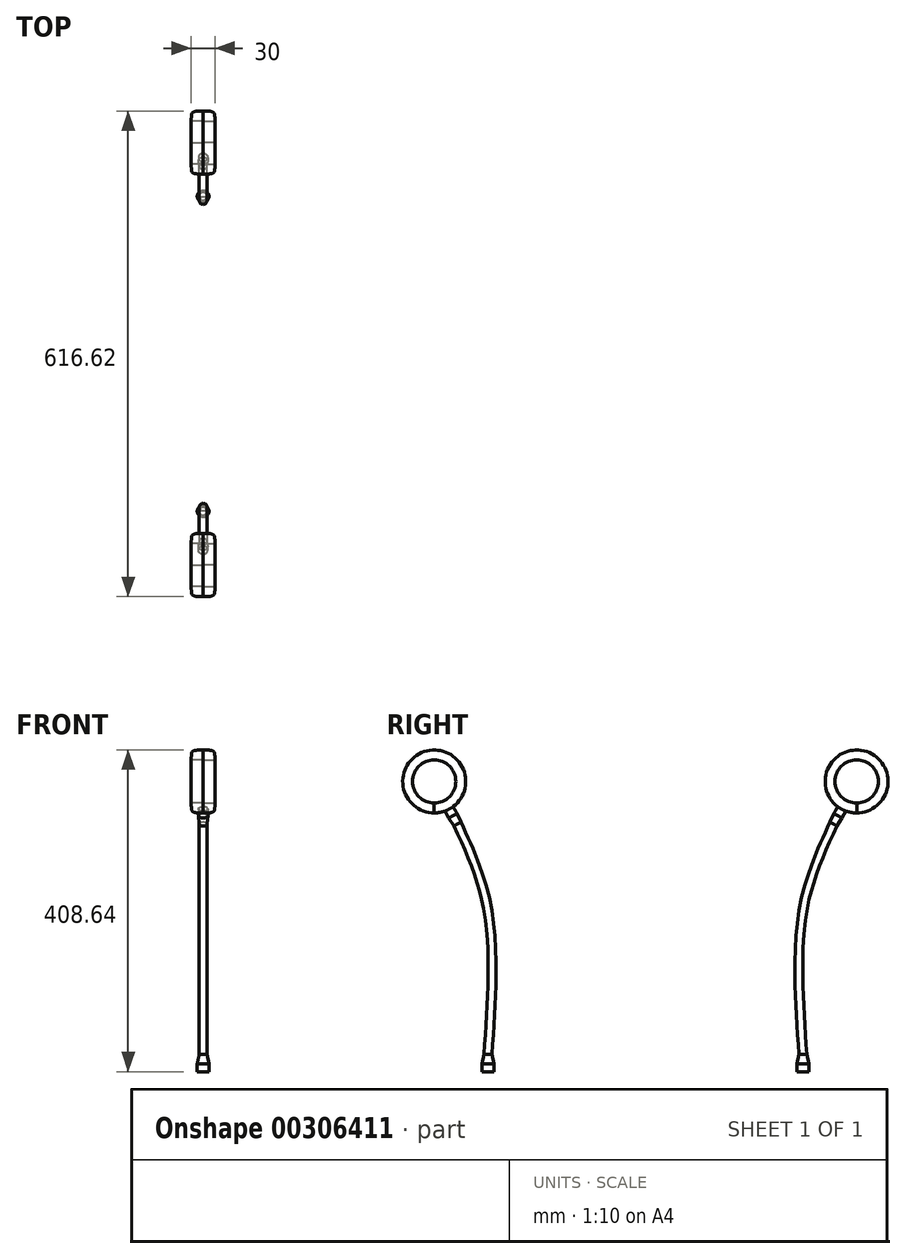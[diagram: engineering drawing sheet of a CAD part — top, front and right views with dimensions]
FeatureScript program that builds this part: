
annotation { "Feature Type Name" : "Feature", "Feature Type Description" : "" }
export const myFeature = defineFeature(function(context is Context, id is Id, definition is map)
    precondition{}
    {
        {
            var Q0;
            Q0=qCreatedBy(makeId("Top.planeOp"),FACE);
            var sketch = newSketch(context, id + "F0", { "sketchPlane" : qUnion([Q0])});
            skCircle(sketch, "E0", {"center": v(0, 0) * mm, "radius": 5 * mm});
            skSolve(sketch);
        }
        {
            var Q0;
            Q0=qCreatedBy(makeId("Right.planeOp"),FACE);
            var sketch = newSketch(context, id + "F1", { "sketchPlane" : qUnion([Q0])});
            skFitSpline(sketch, "E1", {"points": [v(0, 0) * mm, v(0, 182.04) * mm, v(-38.83, 292.58) * mm], "startDerivative": vector(24.2, 350.21) * mm, "endDerivative": vector(-106.66, 230.56) * mm});
            skSolve(sketch);
        }
        {
            var Q0;
            Q0=makeQuery(id+"F0.imprint","IMPRINT",FACE,{"disambiguationData":[TD([[makeQuery(id+"F0.imprint","IMPRINT",EDGE,{"derivedFrom":sQuery(id+"F0.wireOp",EDGE,"E0")}),1.0]])]});
            var Q1;
            Q1=sQuery(id+"F1.wireOp",EDGE,"E1");
            sweep(context, id + "F2", {"profiles" : qUnion([Q0]), "path" : qUnion([Q1])});
        }
        {
            var Q0;
            Q0=qCreatedBy(makeId("Right.planeOp"),FACE);
            var sketch = newSketch(context, id + "F3", { "sketchPlane" : qUnion([Q0])});
            skLineSegment(sketch, "E2", {"start": v(0, 0) * mm, "end": v(-4.82, 0) * mm});
            skLineSegment(sketch, "E3", {"start": v(-4.82, 0) * mm, "end": v(-7.43, -12) * mm});
            skLineSegment(sketch, "E4", {"start": v(-7.43, -12) * mm, "end": v(-7.43, -22) * mm});
            skLineSegment(sketch, "E5", {"start": v(-7.43, -22) * mm, "end": v(0, -22) * mm});
            skLineSegment(sketch, "E6", {"start": v(0, -22) * mm, "end": v(0, 0) * mm});
            skSolve(sketch);
        }
        {
            var Q0;
            Q0=makeQuery(id+"F3.imprint","IMPRINT",FACE,{"disambiguationData":[TD([[makeQuery(id+"F3.imprint","IMPRINT",EDGE,{"derivedFrom":sQuery(id+"F3.wireOp",EDGE,"E2")}),1.0]])]});
            var Q1;
            Q1=sQuery(id+"F3.wireOp",EDGE,"E6");
            revolve(context, id + "F4", {"entities" : qUnion([Q0]), "axis" : qUnion([Q1]), "revolveType" : RevolveType.FULL});
        }
        {
            var Q0;
            Q0=makeQuery(id+"F2.opSweep","CAP_FACE",FACE,{"disambiguationData":[OSD([sQuery(id+"F0.wireOp",EDGE,"E0"),sQuery(id+"F1.wireOp",VERTEX,"E1.end")])],"isStart":false});
            var sketch = newSketch(context, id + "F5", { "sketchPlane" : qUnion([Q0])});
            skLineSegment(sketch, "E7", {"start": v(-3.68, 103.43) * mm, "end": v(0, 106.81) * mm});
            skSolve(sketch);
        }
        {
            var Q0;
            Q0=sQuery(id+"F5.wireOp",EDGE,"E7");
            var Q1;
            Q1=makeQuery(id+"F5.imprint","IMPRINT",FACE,{"disambiguationData":[TD([[makeQuery(id+"F5.imprint","IMPRINT",EDGE,{"derivedFrom":makeQuery(id+"F2.opSweep","CAP_EDGE",EDGE,{"disambiguationData":[OSD([sQuery(id+"F0.wireOp",EDGE,"E0"),sQuery(id+"F1.wireOp",VERTEX,"E1.end")])],"isStart":false})}),1.0]])]});
            cPlane(context, id + "F6", {"entities" : qUnion([Q0, Q1]), "cplaneType" : CPlaneType.LINE_ANGLE, "offset" : 25 * mm, "angle" : 90 * degree, "oppositeDirection" : true, "width" : 150 * mm, "height" : 150 * mm});
        }
        {
            var Q0;
            Q0=qCreatedBy(id+"F6.planeOp",FACE);
            var sketch = newSketch(context, id + "F7", { "sketchPlane" : qUnion([Q0])});
            skLineSegment(sketch, "E8.0", {"start": v(-121, 256.1) * mm, "end": v(-117.12, 259.26) * mm});
            skLineSegment(sketch, "E9", {"start": v(-117.12, 259.26) * mm, "end": v(-130.98, 276.34) * mm});
            skLineSegment(sketch, "E10", {"start": v(-130.98, 276.34) * mm, "end": v(-135.64, 272.57) * mm});
            skLineSegment(sketch, "E11", {"start": v(-135.64, 272.57) * mm, "end": v(-129.34, 264.8) * mm});
            skLineSegment(sketch, "E12", {"start": v(-129.34, 264.8) * mm, "end": v(-121, 256.1) * mm});
            skSolve(sketch);
        }
        {
            var Q0;
            Q0=makeQuery(id+"F7.imprint","IMPRINT",FACE,{"disambiguationData":[TD([[makeQuery(id+"F7.imprint","IMPRINT",EDGE,{"derivedFrom":sQuery(id+"F7.wireOp",EDGE,"E8.0")}),1.0]])]});
            var Q1;
            Q1=sQuery(id+"F7.wireOp",EDGE,"E9");
            revolve(context, id + "F8", {"operationType" : NewBodyOperationType.ADD, "entities" : qUnion([Q0]), "axis" : qUnion([Q1]), "revolveType" : RevolveType.FULL});
        }
        {
            var Q0;
            Q0=qCreatedBy(makeId("Right.planeOp"),FACE);
            var sketch = newSketch(context, id + "F9", { "sketchPlane" : qUnion([Q0])});
            skLineSegment(sketch, "E13", {"start": v(-54.68, 308.97) * mm, "end": v(-44.17, 314.75) * mm});
            skLineSegment(sketch, "E14.0", {"start": v(-44.17, 314.75) * mm, "end": v(-54.68, 308.97) * mm});
            skLineSegment(sketch, "E15", {"start": v(-54.35, 309.16) * mm, "end": v(-54.66, 308.98) * mm});
            skLineSegment(sketch, "E16", {"start": v(-54.66, 308.98) * mm, "end": v(-49.42, 311.86) * mm});
            skCircle(sketch, "E17", {"center": v(-68.3, 346.64) * mm, "radius": 40 * mm});
            skPoint(sketch, "E17.third.point", {"position": v(-48.55, 311.86) * mm});
            skCircle(sketch, "E18", {"center": v(-68.3, 346.64) * mm, "radius": 27.5 * mm});
            skCircle(sketch, "E19.0", {"center": v(-68.3, 346.64) * mm, "radius": 34.5 * mm});
            skSolve(sketch);
        }
        {
            var Q0;
            Q0=sQuery(id+"F9.wireOp",EDGE,"E17");
            extrude(context, id + "F10", {"bodyType" : ToolBodyType.SURFACE, "surfaceEntities" : qUnion([Q0]), "endBound" : BoundingType.SYMMETRIC, "depth" : 2 * mm});
        }
        {
            var Q0;
            Q0=qCreatedBy(makeId("Front.planeOp"),FACE);
            var Q1;
            Q1=sQuery(id+"F9.wireOp",VERTEX,"E17.center");
            cPlane(context, id + "F11", {"entities" : qUnion([Q0, Q1]), "cplaneType" : CPlaneType.PLANE_POINT, "offset" : 25 * mm, "width" : 150 * mm, "height" : 150 * mm});
        }
        {
            var Q0;
            Q0=qCreatedBy(id+"F11.planeOp",FACE);
            var sketch = newSketch(context, id + "F12", { "sketchPlane" : qUnion([Q0])});
            skLineSegment(sketch, "E20.0", {"start": v(15, 386.64) * mm, "end": v(15, 318.64) * mm});
            skFitSpline(sketch, "E21", {"points": [v(15, 319.14) * mm, v(0, 306.64) * mm], "startDerivative": vector(0, -36.76) * mm, "endDerivative": vector(-45, 0) * mm});
            skLineSegment(sketch, "E22", {"start": v(14.5, 319.14) * mm, "end": v(0, 319.14) * mm});
            skLineSegment(sketch, "E23", {"start": v(0, 319.14) * mm, "end": v(0, 306.64) * mm});
            skArc(sketch, "E24.filletArc", {"start": v(15, 318.64) * mm, "mid": v(14.85, 319) * mm, "end": v(14.5, 319.14) * mm});
            skLineSegment(sketch, "E25", {"start": v(0, 346.64) * mm, "end": v(10.62, 346.64) * mm});
            skPoint(sketch, "E26.0.start.orphan", {"position": v(0, 386.64) * mm});
            skPoint(sketch, "E27.0.start.orphan", {"position": v(15, 374.14) * mm});
            skSolve(sketch);
        }
        {
            var Q0;
            Q0=makeQuery(id+"F12.imprint","IMPRINT",FACE,{"disambiguationData":[TD([[makeQuery(id+"F12.imprint","IMPRINT",EDGE,{"derivedFrom":sQuery(id+"F12.wireOp",EDGE,"E21")}),-1.0]])]});
            var Q1;
            Q1=sQuery(id+"F12.wireOp",EDGE,"E25");
            revolve(context, id + "F13", {"operationType" : NewBodyOperationType.ADD, "entities" : qUnion([Q0]), "axis" : qUnion([Q1]), "revolveType" : RevolveType.FULL});
        }
        {
            var Q0;
            Q0=makeQuery(id+"F2.opSweep","SWEPT_BODY",BODY,{"disambiguationData":[OSD([sQuery(id+"F0.wireOp",EDGE,"E0"),sQuery(id+"F1.wireOp",EDGE,"E1")])]});
            var Q1;
            Q1=makeQuery(id+"F9.imprint","IMPRINT",FACE,{"disambiguationData":[TD([[makeQuery(id+"F9.imprint","IMPRINT",EDGE,{"derivedFrom":sQuery(id+"F9.wireOp",EDGE,"E19.0")}),-1.0]])]});
            mirror(context, id + "F14", {"entities" : qUnion([Q0]), "mirrorPlane" : qUnion([Q1])});
        }
        {
            var Q0;
            Q0=qCreatedBy(makeId("Front.planeOp"),FACE);
            cPlane(context, id + "F15", {"entities" : qUnion([Q0]), "cplaneType" : CPlaneType.OFFSET, "offset" : 200 * mm, "oppositeDirection" : true, "width" : 150 * mm, "height" : 150 * mm});
        }
        {
            var Q0;
            Q0=makeQuery(id+"F14.opPattern","COPY",BODY,{"derivedFrom":makeQuery(id+"F2.opSweep","SWEPT_BODY",BODY,{"disambiguationData":[OSD([sQuery(id+"F0.wireOp",EDGE,"E0"),sQuery(id+"F1.wireOp",EDGE,"E1")])]}),"instanceName":"1"});
            var Q1;
            Q1=makeQuery(id+"F10.opExtrude","SWEPT_BODY",BODY,{"disambiguationData":[OSD([sQuery(id+"F9.wireOp",EDGE,"E17")])]});
            var Q2;
            Q2=makeQuery(id+"F2.opSweep","SWEPT_BODY",BODY,{"disambiguationData":[OSD([sQuery(id+"F0.wireOp",EDGE,"E0"),sQuery(id+"F1.wireOp",EDGE,"E1")])]});
            var Q3;
            Q3=makeQuery(id+"F4.opRevolve","SWEPT_BODY",BODY,{"disambiguationData":[OSD([sQuery(id+"F3.wireOp",EDGE,"E2"),sQuery(id+"F3.wireOp",EDGE,"E3"),sQuery(id+"F3.wireOp",EDGE,"E4"),sQuery(id+"F3.wireOp",EDGE,"E5"),sQuery(id+"F3.wireOp",EDGE,"E6")])]});
            var Q4;
            Q4=qCreatedBy(id+"F15.planeOp",FACE);
            mirror(context, id + "F16", {"entities" : qUnion([Q0, Q1, Q2, Q3]), "mirrorPlane" : qUnion([Q4])});
        }
    });
